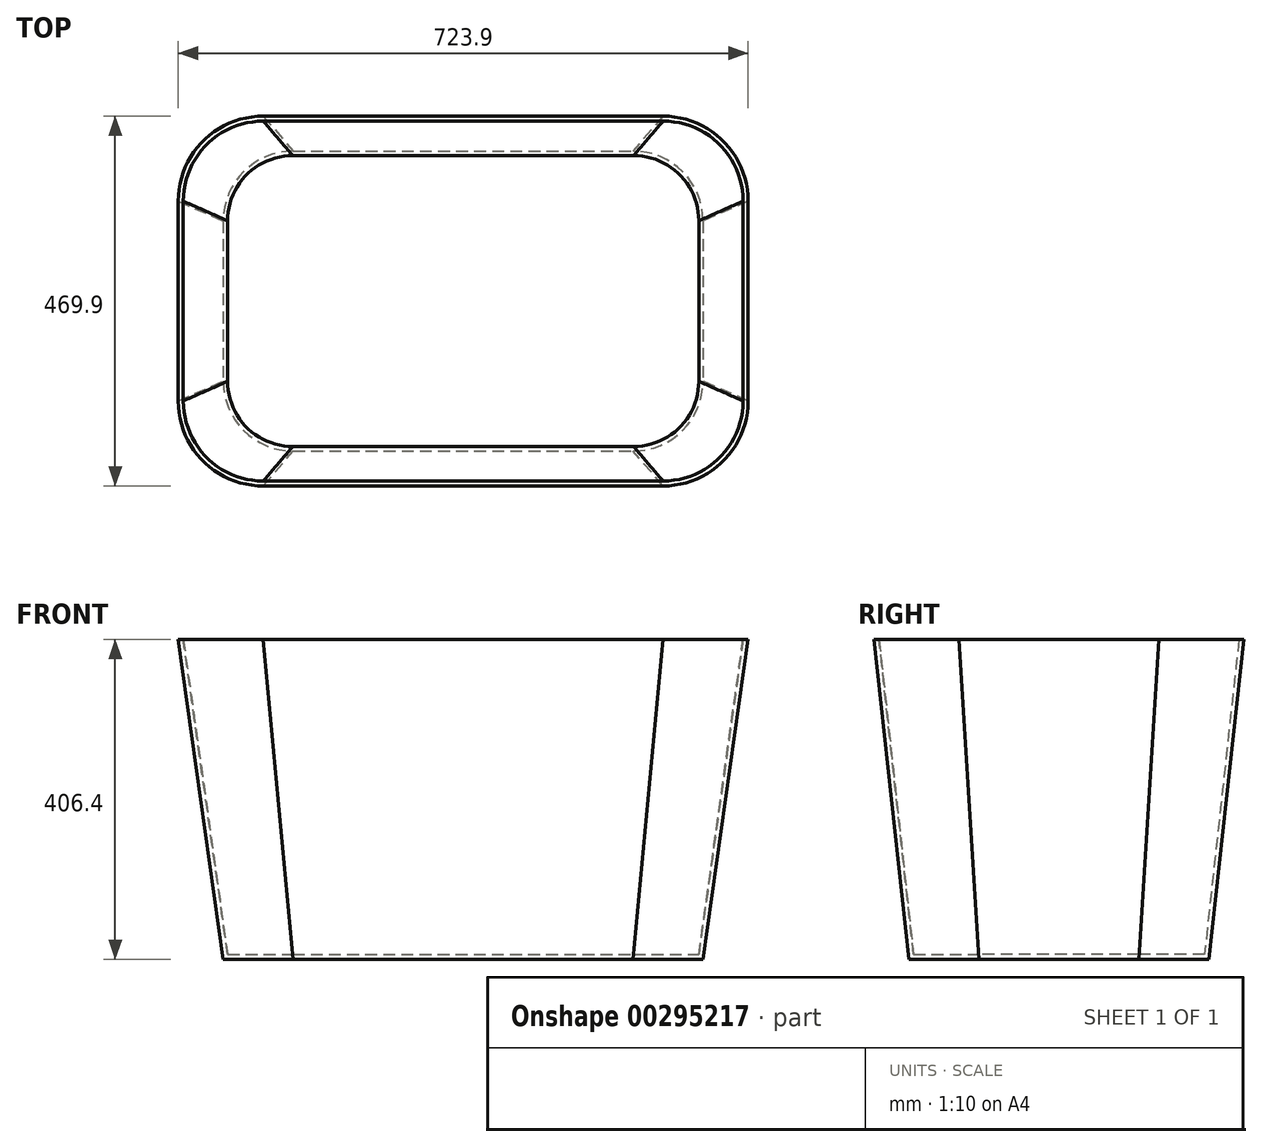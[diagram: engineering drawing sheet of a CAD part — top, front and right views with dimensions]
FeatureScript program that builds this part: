
annotation { "Feature Type Name" : "Feature", "Feature Type Description" : "" }
export const myFeature = defineFeature(function(context is Context, id is Id, definition is map)
    precondition{}
    {
        {
            var Q0;
            Q0=qCreatedBy(makeId("Top.planeOp"),FACE);
            var sketch = newSketch(context, id + "F0", { "sketchPlane" : qUnion([Q0])});
            skPoint(sketch, "E0.middle", {"position": v(0, 0) * mm});
            skPoint(sketch, "E1.visualSharp", {"position": v(-355.6, 228.6) * mm});
            skPoint(sketch, "E2.visualSharp", {"position": v(355.6, 228.6) * mm});
            skPoint(sketch, "E3.visualSharp", {"position": v(355.6, -228.6) * mm});
            skPoint(sketch, "E4.visualSharp", {"position": v(-355.6, -228.6) * mm});
            skLineSegment(sketch, "E5.0", {"start": v(361.95, 127) * mm, "end": v(361.95, -127) * mm});
            skArc(sketch, "E5.1", {"start": v(254, -234.95) * mm, "mid": v(330.33, -203.33) * mm, "end": v(361.95, -127) * mm});
            skArc(sketch, "E5.2", {"start": v(361.95, 127) * mm, "mid": v(330.33, 203.33) * mm, "end": v(254, 234.95) * mm});
            skLineSegment(sketch, "E5.3", {"start": v(-254, -234.95) * mm, "end": v(254, -234.95) * mm});
            skLineSegment(sketch, "E5.4", {"start": v(-254, 234.95) * mm, "end": v(254, 234.95) * mm});
            skArc(sketch, "E5.5", {"start": v(-254, 234.95) * mm, "mid": v(-330.33, 203.33) * mm, "end": v(-361.95, 127) * mm});
            skLineSegment(sketch, "E5.6", {"start": v(-361.95, 127) * mm, "end": v(-361.95, -127) * mm});
            skArc(sketch, "E5.7", {"start": v(-361.95, -127) * mm, "mid": v(-330.33, -203.33) * mm, "end": v(-254, -234.95) * mm});
            skSolve(sketch);
        }
        {
            var Q0;
            Q0=makeQuery(id+"F0.imprint","IMPRINT",FACE,{"disambiguationData":[TD([[makeQuery(id+"F0.imprint","IMPRINT",EDGE,{"derivedFrom":sQuery(id+"F0.wireOp",EDGE,"E5.0")}),-1.0]])]});
            extrude(context, id + "F1", {"entities" : qUnion([Q0]), "depth" : 406.4 * mm});
        }
        {
            var Q0;
            Q0=makeQuery(id+"F1.opExtrude","CAP_FACE",FACE,{"disambiguationData":[OSD([sQuery(id+"F0.wireOp",EDGE,"E0.bottom"),sQuery(id+"F0.wireOp",EDGE,"E0.top"),sQuery(id+"F0.wireOp",EDGE,"E0.left"),sQuery(id+"F0.wireOp",EDGE,"E0.right"),sQuery(id+"F0.wireOp",EDGE,"E1.filletArc"),sQuery(id+"F0.wireOp",EDGE,"E2.filletArc"),sQuery(id+"F0.wireOp",EDGE,"E3.filletArc"),sQuery(id+"F0.wireOp",EDGE,"E4.filletArc"),sQuery(id+"F0.wireOp",EDGE,"E5.0"),sQuery(id+"F0.wireOp",EDGE,"E5.1"),sQuery(id+"F0.wireOp",EDGE,"E5.2"),sQuery(id+"F0.wireOp",EDGE,"E5.3"),sQuery(id+"F0.wireOp",EDGE,"E5.4"),sQuery(id+"F0.wireOp",EDGE,"E5.5"),sQuery(id+"F0.wireOp",EDGE,"E5.6"),sQuery(id+"F0.wireOp",EDGE,"E5.7")])],"isStart":true});
            var sketch = newSketch(context, id + "F2", { "sketchPlane" : qUnion([Q0])});
            skLineSegment(sketch, "E6.bottom", {"start": v(-215.9, -190.5) * mm, "end": v(215.9, -190.5) * mm});
            skLineSegment(sketch, "E6.top", {"start": v(-215.9, 190.5) * mm, "end": v(215.9, 190.5) * mm});
            skLineSegment(sketch, "E6.left", {"start": v(-304.8, -101.6) * mm, "end": v(-304.8, 101.6) * mm});
            skLineSegment(sketch, "E6.right", {"start": v(304.8, -101.6) * mm, "end": v(304.8, 101.6) * mm});
            skPoint(sketch, "E6.middle", {"position": v(0, 0) * mm});
            skPoint(sketch, "E7.visualSharp", {"position": v(-304.8, 190.5) * mm});
            skArc(sketch, "E7.filletArc", {"start": v(-215.9, 190.5) * mm, "mid": v(-278.76, 164.46) * mm, "end": v(-304.8, 101.6) * mm});
            skPoint(sketch, "E8.visualSharp", {"position": v(304.8, 190.5) * mm});
            skArc(sketch, "E8.filletArc", {"start": v(304.8, 101.6) * mm, "mid": v(278.76, 164.46) * mm, "end": v(215.9, 190.5) * mm});
            skPoint(sketch, "E9.visualSharp", {"position": v(304.8, -190.5) * mm});
            skArc(sketch, "E9.filletArc", {"start": v(215.9, -190.5) * mm, "mid": v(278.76, -164.46) * mm, "end": v(304.8, -101.6) * mm});
            skPoint(sketch, "E10.visualSharp", {"position": v(-304.8, -190.5) * mm});
            skArc(sketch, "E10.filletArc", {"start": v(-304.8, -101.6) * mm, "mid": v(-278.76, -164.46) * mm, "end": v(-215.9, -190.5) * mm});
            skSolve(sketch);
        }
        {
            var Q1;
            Q1=makeQuery(id+"F1.opExtrude","CAP_FACE",FACE,{"disambiguationData":[OSD([sQuery(id+"F0.wireOp",EDGE,"E5.0"),sQuery(id+"F0.wireOp",EDGE,"E5.1"),sQuery(id+"F0.wireOp",EDGE,"E5.2"),sQuery(id+"F0.wireOp",EDGE,"E5.3"),sQuery(id+"F0.wireOp",EDGE,"E5.4"),sQuery(id+"F0.wireOp",EDGE,"E5.5"),sQuery(id+"F0.wireOp",EDGE,"E5.6"),sQuery(id+"F0.wireOp",EDGE,"E5.7")])],"isStart":false});
            var Q2;
            Q2=makeQuery(id+"F2.imprint","IMPRINT",FACE,{"disambiguationData":[TD([[makeQuery(id+"F2.imprint","IMPRINT",EDGE,{"derivedFrom":sQuery(id+"F2.wireOp",EDGE,"E6.bottom")}),1.0]])]});
            loft(context, id + "F3", {"operationType" : NewBodyOperationType.INTERSECT, "sheetProfilesArray" : [{ "sheetProfileEntities" : qUnion([Q1]) }, { "sheetProfileEntities" : qUnion([Q2]) }]});
        }
        {
            var Q0;
            Q0=makeQuery(id+"F1.opExtrude","CAP_FACE",FACE,{"disambiguationData":[OSD([sQuery(id+"F0.wireOp",EDGE,"E5.0"),sQuery(id+"F0.wireOp",EDGE,"E5.1"),sQuery(id+"F0.wireOp",EDGE,"E5.2"),sQuery(id+"F0.wireOp",EDGE,"E5.3"),sQuery(id+"F0.wireOp",EDGE,"E5.4"),sQuery(id+"F0.wireOp",EDGE,"E5.5"),sQuery(id+"F0.wireOp",EDGE,"E5.6"),sQuery(id+"F0.wireOp",EDGE,"E5.7")])],"isStart":false});
            shell(context, id + "F4", {"entities" : qUnion([Q0]), "thickness" : 6.35 * mm});
        }
    });
